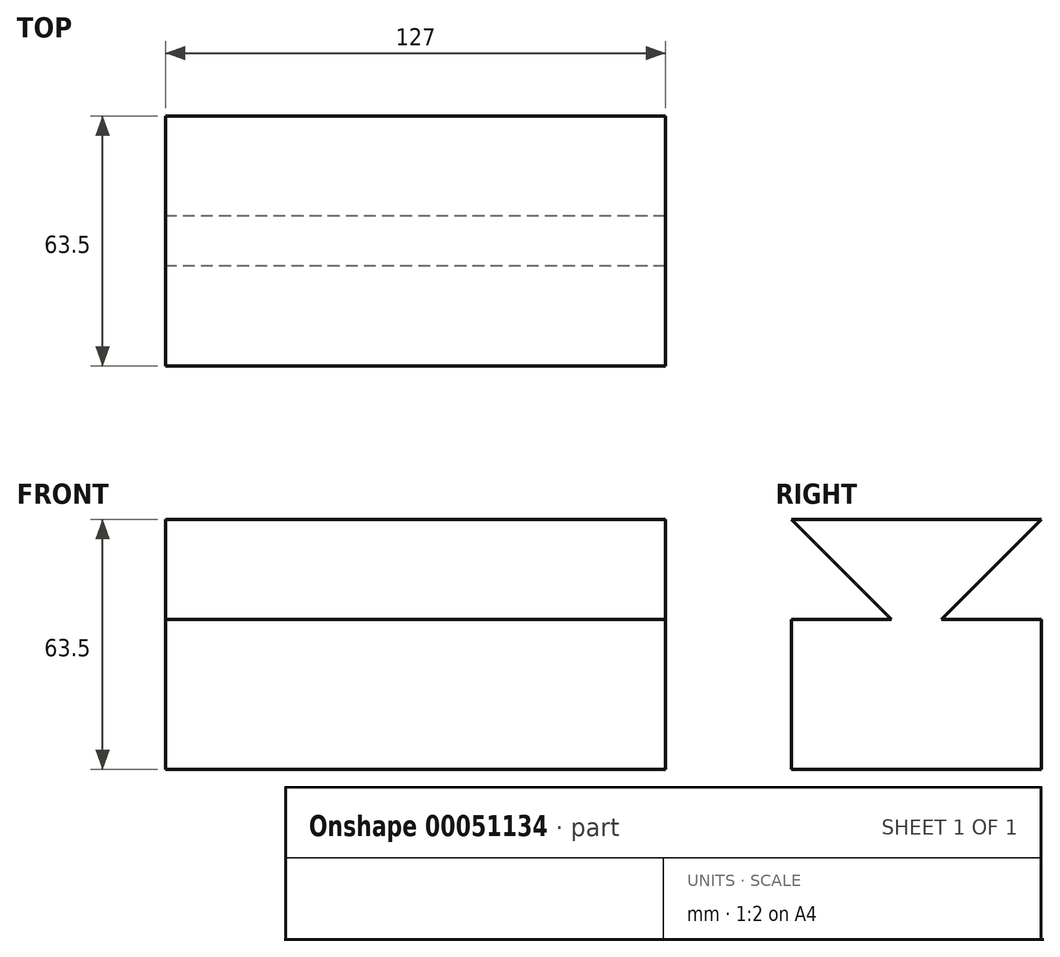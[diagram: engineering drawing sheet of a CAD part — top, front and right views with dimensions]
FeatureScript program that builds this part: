
annotation { "Feature Type Name" : "Feature", "Feature Type Description" : "" }
export const myFeature = defineFeature(function(context is Context, id is Id, definition is map)
    precondition{}
    {
        {
            var Q0;
            Q0=qCreatedBy(makeId("Right.planeOp"),FACE);
            var sketch = newSketch(context, id + "F0", { "sketchPlane" : qUnion([Q0])});
            skLineSegment(sketch, "E0.rect.bottom", {"start": v(31.75, 31.75) * mm, "end": v(-31.75, 31.75) * mm});
            skLineSegment(sketch, "E0.rect.top", {"start": v(31.75, -31.75) * mm, "end": v(-31.75, -31.75) * mm});
            skLineSegment(sketch, "E0.rect.left", {"start": v(31.75, 6.35) * mm, "end": v(31.75, -31.75) * mm});
            skLineSegment(sketch, "E0.rect.right", {"start": v(-31.75, 6.35) * mm, "end": v(-31.75, -31.75) * mm});
            skPoint(sketch, "E0.rect.middle", {"position": v(0, 0) * mm});
            skLineSegment(sketch, "E1", {"start": v(-31.75, 6.35) * mm, "end": v(-6.35, 6.35) * mm});
            skLineSegment(sketch, "E2", {"start": v(-31.75, 31.75) * mm, "end": v(-6.35, 6.35) * mm});
            skLineSegment(sketch, "E3", {"start": v(31.75, 31.75) * mm, "end": v(6.35, 6.35) * mm});
            skLineSegment(sketch, "E4.trimOffspring", {"start": v(6.35, 6.35) * mm, "end": v(31.75, 6.35) * mm});
            skSolve(sketch);
        }
        {
            var Q0;
            Q0 = qSketchRegion(id + "F0", true);
            extrude(context, id + "F1", {"entities" : qUnion([Q0]), "depth" : 63.5 * mm, "hasSecondDirection" : true, "secondDirectionOppositeDirection" : true, "secondDirectionDepth" : 63.5 * mm});
        }
    });
